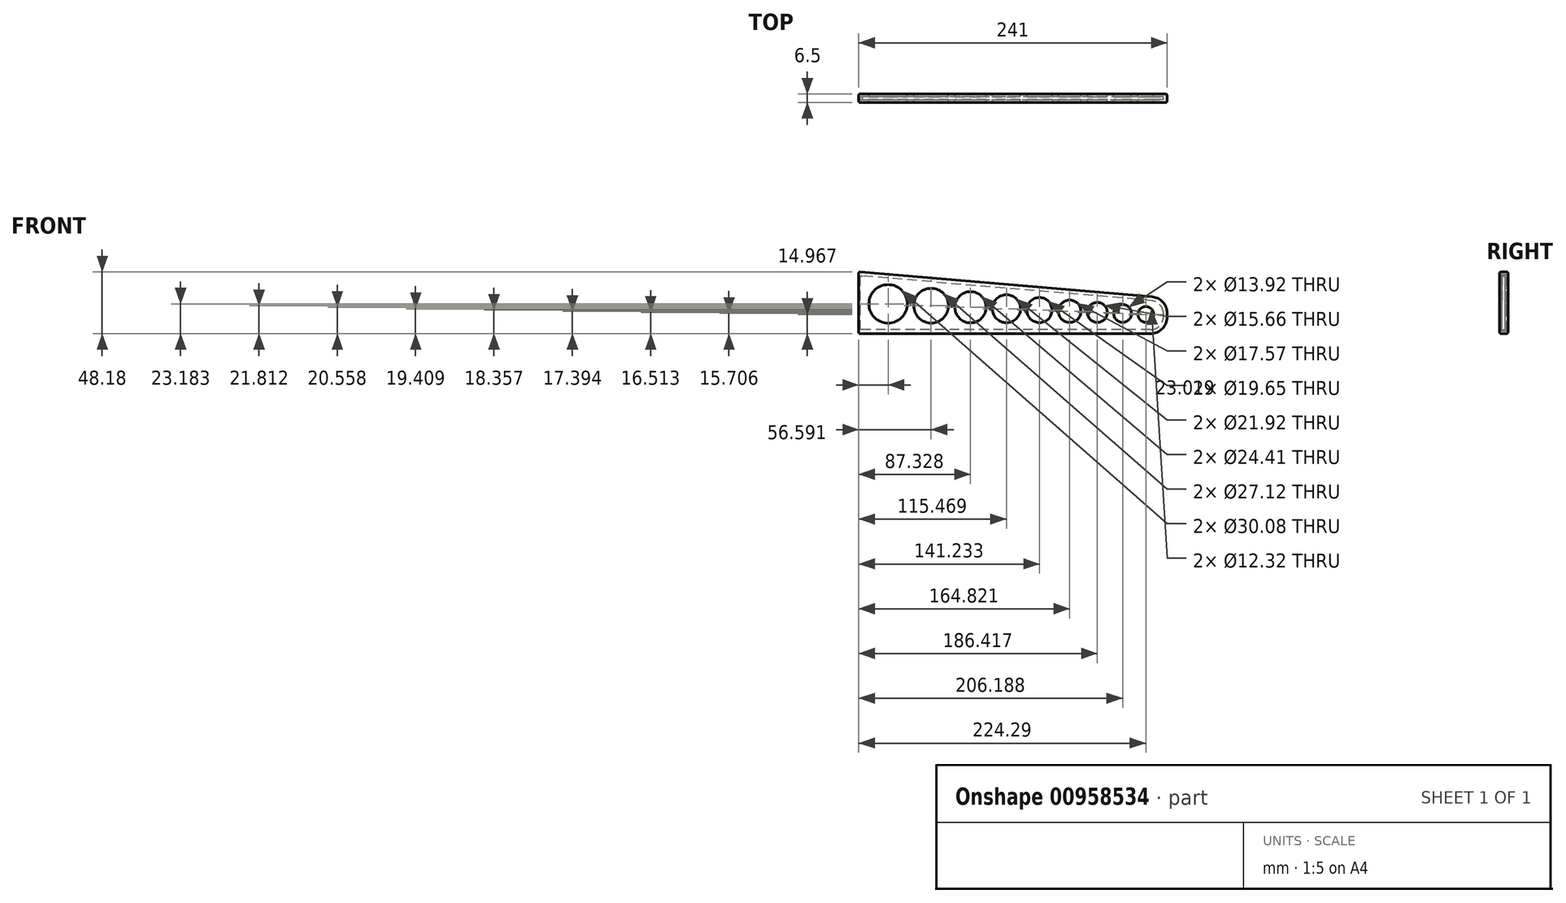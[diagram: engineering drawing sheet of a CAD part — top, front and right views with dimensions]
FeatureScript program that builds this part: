
annotation { "Feature Type Name" : "Feature", "Feature Type Description" : "" }
export const myFeature = defineFeature(function(context is Context, id is Id, definition is map)
    precondition{}
    {
        {
            var Q0;
            Q0=qCreatedBy(makeId("Front.planeOp"),FACE);
            var sketch = newSketch(context, id + "F0", { "sketchPlane" : qUnion([Q0])});
            skLineSegment(sketch, "E0", {"start": v(-120.2, 0) * mm, "end": v(104.8, 0) * mm});
            skLineSegment(sketch, "E1", {"start": v(114.8, 10) * mm, "end": v(114.8, 12.81) * mm});
            skLineSegment(sketch, "E2", {"start": v(-120.2, 0) * mm, "end": v(-120.2, 42) * mm});
            skLineSegment(sketch, "E3", {"start": v(-120.2, 42) * mm, "end": v(105.64, 22.78) * mm});
            skPoint(sketch, "E4.visualSharp", {"position": v(114.8, 22) * mm});
            skArc(sketch, "E4.filletArc", {"start": v(114.8, 12.81) * mm, "mid": v(112.16, 19.58) * mm, "end": v(105.64, 22.78) * mm});
            skPoint(sketch, "E5.visualSharp", {"position": v(114.8, 0) * mm});
            skArc(sketch, "E5.filletArc", {"start": v(104.8, 0) * mm, "mid": v(111.87, 2.93) * mm, "end": v(114.8, 10) * mm});
            skLineSegment(sketch, "E6.0", {"start": v(-123.2, -3) * mm, "end": v(104.8, -3) * mm});
            skLineSegment(sketch, "E6.1", {"start": v(-123.2, 45.27) * mm, "end": v(105.9, 25.77) * mm});
            skArc(sketch, "E6.2", {"start": v(117.8, 12.81) * mm, "mid": v(114.37, 21.6) * mm, "end": v(105.9, 25.77) * mm});
            skLineSegment(sketch, "E6.3", {"start": v(-123.2, -3) * mm, "end": v(-123.2, 45.27) * mm});
            skLineSegment(sketch, "E6.4", {"start": v(117.8, 10) * mm, "end": v(117.8, 12.81) * mm});
            skArc(sketch, "E6.5", {"start": v(104.8, -3) * mm, "mid": v(113.99, 0.8) * mm, "end": v(117.8, 10) * mm});
            skLineSegment(sketch, "E7", {"start": v(-120.2, 42) * mm, "end": v(-123.2, 42) * mm});
            skLineSegment(sketch, "E8", {"start": v(-120.2, 0) * mm, "end": v(-123.2, 0) * mm});
            skPoint(sketch, "E9", {"position": v(-120.2, 21) * mm});
            skPoint(sketch, "E10", {"position": v(114.8, 11.4) * mm});
            skLineSegment(sketch, "E11", {"start": v(114.8, 11.4) * mm, "end": v(-120.2, 21) * mm, "construction": true});
            skCircle(sketch, "E12", {"center": v(-100.18, 20.18) * mm, "radius": 15.04 * mm});
            skCircle(sketch, "E13", {"center": v(-66.6, 18.81) * mm, "radius": 13.56 * mm});
            skCircle(sketch, "E14", {"center": v(-35.87, 17.56) * mm, "radius": 12.2 * mm});
            skCircle(sketch, "E15", {"center": v(-7.73, 16.4) * mm, "radius": 10.96 * mm});
            skCircle(sketch, "E16", {"center": v(18.03, 15.36) * mm, "radius": 9.82 * mm});
            skCircle(sketch, "E17", {"center": v(41.62, 14.4) * mm, "radius": 8.78 * mm});
            skCircle(sketch, "E18", {"center": v(63.22, 13.51) * mm, "radius": 7.83 * mm});
            skCircle(sketch, "E19", {"center": v(82.99, 12.7) * mm, "radius": 6.96 * mm});
            skCircle(sketch, "E20", {"center": v(101.1, 11.97) * mm, "radius": 6.16 * mm});
            skSolve(sketch);
        }
        {
            var Q0;
            Q0=makeQuery(id+"F0.imprint","IMPRINT",FACE,{"disambiguationData":[TD([[makeQuery(id+"F0.imprint","IMPRINT",EDGE,{"derivedFrom":sQuery(id+"F0.wireOp",EDGE,"E2")}),1.0]])]});
            var Q1;
            Q1=makeQuery(id+"F0.imprint","IMPRINT",FACE,{"disambiguationData":[TD([[makeQuery(id+"F0.imprint","IMPRINT",EDGE,{"derivedFrom":sQuery(id+"F0.wireOp",EDGE,"E0")}),-1.0]])]});
            var Q2;
            Q2=makeQuery(id+"F0.imprint","IMPRINT",FACE,{"disambiguationData":[TD([[makeQuery(id+"F0.imprint","IMPRINT",EDGE,{"derivedFrom":sQuery(id+"F0.wireOp",EDGE,"E0")}),1.0]])]});
            extrude(context, id + "F1", {"entities" : qUnion([Q0, Q1, Q2]), "depth" : 2 * mm, "offsetDistance" : 25 * mm});
        }
        {
            var Q0;
            Q0=makeQuery(id+"F0.imprint","IMPRINT",FACE,{"disambiguationData":[TD([[makeQuery(id+"F0.imprint","IMPRINT",EDGE,{"derivedFrom":sQuery(id+"F0.wireOp",EDGE,"E0")}),-1.0]])]});
            extrude(context, id + "F2", {"entities" : qUnion([Q0]), "operationType" : NewBodyOperationType.ADD, "depth" : 4.5 * mm, "offsetDistance" : 25 * mm});
        }
        {
            var Q0;
            Q0=makeQuery(id+"F0.imprint","IMPRINT",FACE,{"disambiguationData":[TD([[makeQuery(id+"F0.imprint","IMPRINT",EDGE,{"derivedFrom":sQuery(id+"F0.wireOp",EDGE,"E0")}),-1.0]])]});
            var Q1;
            Q1=makeQuery(id+"F0.imprint","IMPRINT",FACE,{"disambiguationData":[TD([[makeQuery(id+"F0.imprint","IMPRINT",EDGE,{"derivedFrom":sQuery(id+"F0.wireOp",EDGE,"E2")}),1.0]])]});
            var Q2;
            Q2=makeQuery(id+"F0.imprint","IMPRINT",FACE,{"disambiguationData":[TD([[makeQuery(id+"F0.imprint","IMPRINT",EDGE,{"derivedFrom":sQuery(id+"F0.wireOp",EDGE,"E0")}),1.0]])]});
            extrude(context, id + "F3", {"entities" : qUnion([Q0, Q1, Q2]), "operationType" : NewBodyOperationType.ADD, "depth" : 6.5 * mm, "offsetDistance" : 25 * mm, "hasSecondDirection" : true, "secondDirectionOppositeDirection" : false, "secondDirectionDepth" : 4.5 * mm});
        }
        {
            var Q0;
            Q0=makeQuery(id+"F3.opExtrude","CAP_EDGE",EDGE,{"disambiguationData":[OSD([sQuery(id+"F0.wireOp",EDGE,"E6.3")])],"isStart":true});
            var Q1;
            Q1=makeQuery(id+"F2.opExtrude","SWEPT_EDGE",EDGE,{"disambiguationData":[OSD([sQuery(id+"F0.wireOp",EDGE,"E6.3"),sQuery(id+"F0.wireOp",EDGE,"E8")])]});
            var Q2;
            Q2=makeQuery(id+"F1.opExtrude","CAP_EDGE",EDGE,{"disambiguationData":[OSD([sQuery(id+"F0.wireOp",EDGE,"E6.3")])],"isStart":false});
            var Q3;
            Q3=makeQuery(id+"F2.opExtrude","SWEPT_EDGE",EDGE,{"disambiguationData":[OSD([sQuery(id+"F0.wireOp",EDGE,"E6.3"),sQuery(id+"F0.wireOp",EDGE,"E7")])]});
            chamfer(context, id + "F4", {"entities" : qUnion([Q0, Q1, Q2, Q3]), "width" : 1 * mm, "tangentPropagation" : true});
        }
        {
            var Q0;
            Q0=makeQuery(id+"F1.opExtrude","CAP_FACE",FACE,{"disambiguationData":[OSD([sQuery(id+"F0.wireOp",EDGE,"E6.0"),sQuery(id+"F0.wireOp",EDGE,"E6.1"),sQuery(id+"F0.wireOp",EDGE,"E6.2"),sQuery(id+"F0.wireOp",EDGE,"E6.3"),sQuery(id+"F0.wireOp",EDGE,"E6.4"),sQuery(id+"F0.wireOp",EDGE,"E6.5"),sQuery(id+"F0.wireOp",EDGE,"E12"),sQuery(id+"F0.wireOp",EDGE,"E13"),sQuery(id+"F0.wireOp",EDGE,"E14"),sQuery(id+"F0.wireOp",EDGE,"E15"),sQuery(id+"F0.wireOp",EDGE,"E16"),sQuery(id+"F0.wireOp",EDGE,"E17"),sQuery(id+"F0.wireOp",EDGE,"E18"),sQuery(id+"F0.wireOp",EDGE,"E19"),sQuery(id+"F0.wireOp",EDGE,"E20")])],"isStart":true});
            var Q1;
            Q1=makeQuery(id+"F3.opExtrude","CAP_FACE",FACE,{"disambiguationData":[OSD([sQuery(id+"F0.wireOp",EDGE,"E6.0"),sQuery(id+"F0.wireOp",EDGE,"E6.1"),sQuery(id+"F0.wireOp",EDGE,"E6.2"),sQuery(id+"F0.wireOp",EDGE,"E6.3"),sQuery(id+"F0.wireOp",EDGE,"E6.4"),sQuery(id+"F0.wireOp",EDGE,"E6.5"),sQuery(id+"F0.wireOp",EDGE,"E12"),sQuery(id+"F0.wireOp",EDGE,"E13"),sQuery(id+"F0.wireOp",EDGE,"E14"),sQuery(id+"F0.wireOp",EDGE,"E15"),sQuery(id+"F0.wireOp",EDGE,"E16"),sQuery(id+"F0.wireOp",EDGE,"E17"),sQuery(id+"F0.wireOp",EDGE,"E18"),sQuery(id+"F0.wireOp",EDGE,"E19"),sQuery(id+"F0.wireOp",EDGE,"E20")])],"isStart":false});
            var Q2;
            {var subQ0=sQuery(id+"F0.wireOp",EDGE,"E6.3");var subQ1=sQuery(id+"F0.wireOp",EDGE,"E6.0");Q2=makeQuery(id+"F3.boolean.opBoolean","MERGE",EDGE,{"derivedFrom":[makeQuery(id+"F2.boolean.opBoolean","MERGE",EDGE,{"derivedFrom":[makeQuery(id+"F1.opExtrude","SWEPT_EDGE",EDGE,{"disambiguationData":[OSD([subQ1,subQ0])]}),makeQuery(id+"F2.opExtrude","SWEPT_EDGE",EDGE,{"disambiguationData":[OSD([subQ1,subQ0])]})]}),makeQuery(id+"F3.opExtrude","SWEPT_EDGE",EDGE,{"disambiguationData":[OSD([subQ1,subQ0])]})]});}
            var Q3;
            {var subQ0=sQuery(id+"F0.wireOp",EDGE,"E6.3");var subQ1=sQuery(id+"F0.wireOp",EDGE,"E6.1");Q3=makeQuery(id+"F3.boolean.opBoolean","MERGE",EDGE,{"derivedFrom":[makeQuery(id+"F2.boolean.opBoolean","MERGE",EDGE,{"derivedFrom":[makeQuery(id+"F1.opExtrude","SWEPT_EDGE",EDGE,{"disambiguationData":[OSD([subQ1,subQ0])]}),makeQuery(id+"F2.opExtrude","SWEPT_EDGE",EDGE,{"disambiguationData":[OSD([subQ1,subQ0])]})]}),makeQuery(id+"F3.opExtrude","SWEPT_EDGE",EDGE,{"disambiguationData":[OSD([subQ1,subQ0])]})]});}
            fillet(context, id + "F5", {"entities" : qUnion([Q0, Q1, Q2, Q3]), "radius" : 1 * mm, "tangentPropagation" : true, "allowEdgeOverflow" : false});
        }
    });
